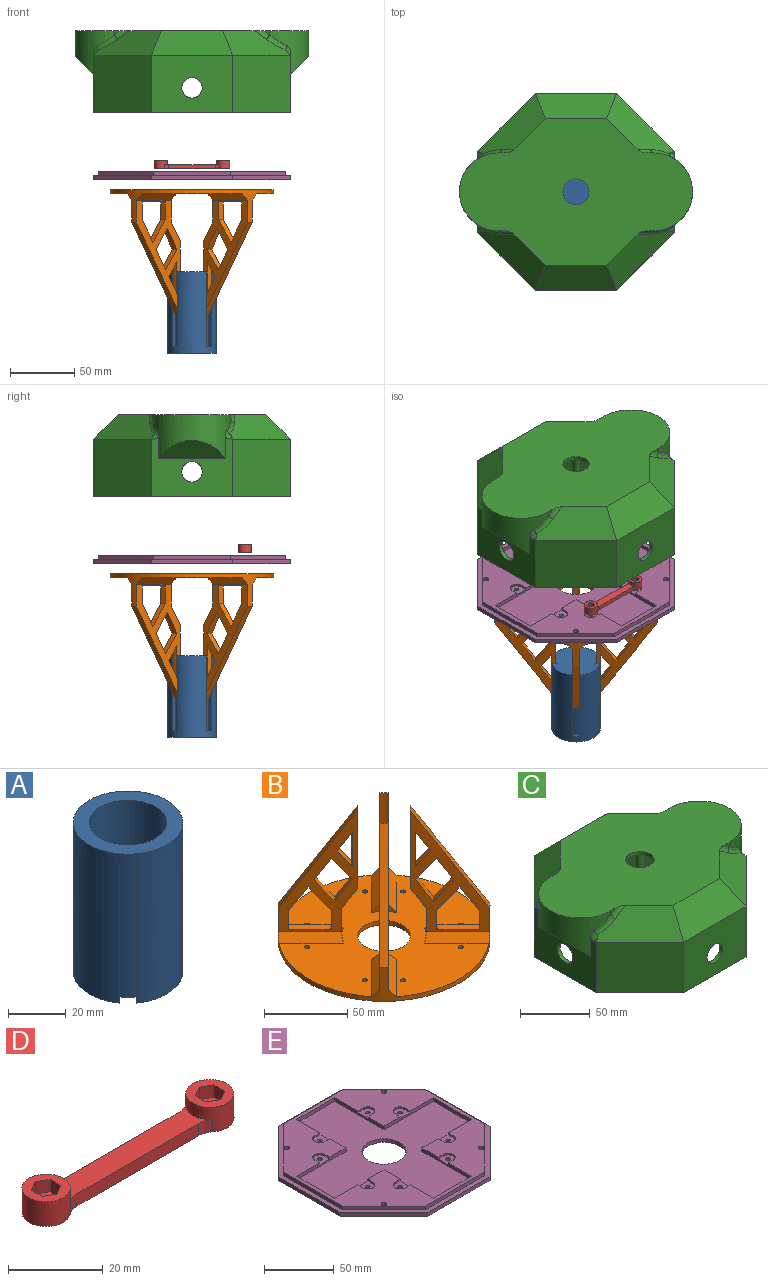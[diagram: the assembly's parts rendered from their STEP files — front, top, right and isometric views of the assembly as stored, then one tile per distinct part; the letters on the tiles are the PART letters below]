
ASSEMBLY  parts=5 mates=4
PART A: 21 faces, bbox 38.1x38.1x63.5 mm
  f0: plane 58.42x2.46mm, normal (0.71,0.71,0), area 203mm2, adj f2,f12,f15,f20
  f1: plane 58.42x2.46mm, normal (-0.71,-0.71,0), area 203mm2, adj f2,f12,f15,f20
  f2: cylinder r=15.62mm len=58.42mm, axis (0,0,-1), area 328.2mm2, adj f0,f1,f15,f20
  f3: plane 58.42x2.46mm, normal (0.71,-0.71,0), area 203mm2, adj f5,f12,f15,f19
  f4: plane 58.42x2.46mm, normal (-0.71,0.71,0), area 203mm2, adj f5,f12,f15,f19
  f5: cylinder r=15.62mm len=58.42mm, axis (0,0,-1), area 328.2mm2, adj f3,f4,f15,f19
  f6: plane 58.42x2.46mm, normal (-0.71,-0.71,0), area 203mm2, adj f8,f12,f15,f18
  f7: plane 58.42x2.46mm, normal (0.71,0.71,0), area 203mm2, adj f8,f12,f15,f18
  f8: cylinder r=15.62mm len=58.42mm, axis (0,0,-1), area 328.2mm2, adj f6,f7,f15,f18
  f9: plane 58.42x2.46mm, normal (0.71,-0.71,0), area 203mm2, adj f11,f12,f15,f17
  f10: plane 58.42x2.46mm, normal (-0.71,0.71,0), area 203mm2, adj f11,f12,f15,f17
  f11: cylinder r=15.62mm len=58.42mm, axis (0,0,-1), area 328.2mm2, adj f9,f10,f15,f17
  f12: cylinder r=19.05mm len=63.5mm, axis (0,0,-1), area 6290.1mm2, adj f0,f1,f3,f4,f6,f7,f9,f10
  f13: cylinder r=13.46mm len=58.42mm, axis (0,0,-1), area 4941.4mm2, adj f14,f16
  f14: plane 38.1x38.1mm, normal (0,0,1), area 570.8mm2, adj f12,f13
  f15: plane 38.1x38.1mm, normal (0,0,-1), area 1063.1mm2, adj f0,f1,f2,f3,f4,f5,f6,f7
  f16: plane 26.92x26.92mm, normal (0,0,1), area 569.3mm2, adj f13
  f17: plane 6.41x6.41mm, normal (0,0,-1), area 19.2mm2, adj f9,f10,f11,f12
  f18: plane 6.41x6.41mm, normal (0,0,-1), area 19.2mm2, adj f6,f7,f8,f12
  f19: plane 6.41x6.41mm, normal (0,0,-1), area 19.2mm2, adj f3,f4,f5,f12
  f20: plane 6.41x6.41mm, normal (0,0,-1), area 19.2mm2, adj f0,f1,f2,f12
PART B: 92 faces, bbox 127.6x127.6x97.7 mm
  f0: plane 89.46x34.37mm, normal (0.71,0.71,0), area 1250.3mm2, adj f9,f13,f17,f28,f29,f30,f31,f32
  f1: plane 88.87x33.78mm, normal (0.71,-0.71,0), area 1250.3mm2, adj f10,f16,f17,f33,f68,f69,f70,f71
  f2: plane 89.46x34.37mm, normal (-0.71,0.71,0), area 1250.3mm2, adj f10,f16,f17,f33,f68,f69,f70,f71
  f3: plane 88.87x33.78mm, normal (0.71,0.71,0), area 1250.3mm2, adj f11,f15,f17,f34,f56,f57,f58,f59
  f4: plane 89.46x34.37mm, normal (-0.71,-0.71,0), area 1250.3mm2, adj f11,f15,f17,f34,f56,f57,f58,f59
  f5: plane 88.87x33.78mm, normal (-0.71,0.71,0), area 1250.3mm2, adj f12,f14,f17,f35,f44,f45,f46,f47
  f6: plane 89.46x34.37mm, normal (0.71,-0.71,0), area 1250.3mm2, adj f12,f14,f17,f35,f44,f45,f46,f47
  f7: plane 88.87x33.78mm, normal (-0.71,-0.71,0), area 1250.3mm2, adj f9,f13,f17,f28,f29,f30,f31,f32
  f8: plane 127x127mm, normal (0,0,1), area 9480.5mm2, adj f17,f18,f19,f20,f21,f22,f23,f24
  f9: revolved ~14.57x12.25mm, area 92.3mm2, adj f0,f7,f32,f83
  f10: revolved ~14.57x12.25mm, area 92.3mm2, adj f1,f2,f33,f80
  f11: revolved ~14.57x12.25mm, area 92.3mm2, adj f3,f4,f34,f81
  f12: revolved ~14.57x12.25mm, area 92.3mm2, adj f5,f6,f35,f82
  f13: revolved ~71.93x46.32mm, area 438.7mm2, adj f0,f7,f17,f83
  f14: revolved ~71.93x46.32mm, area 438.7mm2, adj f5,f6,f17,f82
  f15: revolved ~71.93x46.32mm, area 438.7mm2, adj f3,f4,f17,f81
  f16: revolved ~71.93x46.32mm, area 438.7mm2, adj f1,f2,f17,f80
  f17: cylinder r=63.5mm len=127mm, axis (0,0,-1), area 1818mm2, adj f0,f1,f2,f3,f4,f5,f6,f7
  f18: cylinder r=1.59mm len=3.18mm, axis (0,0,-1), area 31.7mm2, adj f8,f26
  f19: cylinder r=1.59mm len=3.18mm, axis (0,0,-1), area 31.7mm2, adj f8,f26
  f20: cylinder r=1.59mm len=3.18mm, axis (0,0,-1), area 31.7mm2, adj f8,f26
  f21: cylinder r=1.59mm len=3.18mm, axis (0,0,-1), area 31.7mm2, adj f8,f26
  f22: cylinder r=1.59mm len=3.18mm, axis (0,0,-1), area 31.7mm2, adj f8,f26
  f23: cylinder r=1.59mm len=3.18mm, axis (0,0,-1), area 31.7mm2, adj f8,f26
  f24: cylinder r=1.59mm len=3.18mm, axis (0,0,-1), area 31.7mm2, adj f8,f26
  f25: cylinder r=1.59mm len=3.18mm, axis (0,0,-1), area 31.7mm2, adj f8,f26
  f26: plane 127x127mm, normal (0,0,-1), area 11812.6mm2, adj f17,f18,f19,f20,f21,f22,f23,f24
  f27: cylinder r=15.88mm len=31.75mm, axis (0,0,-1), area 316.7mm2, adj f8,f26
  f28: revolved ~15.83x12.12mm, area 97.9mm2, adj f0,f7,f29,f31
  f29: revolved ~15.82x13.69mm, area 104mm2, adj f0,f7,f28,f30
  f30: revolved ~15.83x12.71mm, area 99.6mm2, adj f0,f7,f29,f31
  f31: revolved ~15.82x14.31mm, area 101.9mm2, adj f0,f7,f28,f30
  f32: cylinder r=25.48mm len=22.02mm, axis (0,0,1), area 138.4mm2, adj f0,f7,f8,f9,f88,f89
  f33: cylinder r=25.48mm len=22.02mm, axis (0,0,1), area 138.4mm2, adj f1,f2,f8,f10,f86,f87
  f34: cylinder r=25.48mm len=22.02mm, axis (0,0,1), area 138.4mm2, adj f3,f4,f8,f11,f84,f85
  f35: cylinder r=25.48mm len=22.02mm, axis (0,0,1), area 138.4mm2, adj f5,f6,f8,f12,f90,f91
  f36: revolved ~11.32x11.26mm, area 74.7mm2, adj f0,f7,f37,f38
  f37: cylinder r=19.22mm len=24.62mm, axis (0,0,1), area 125.4mm2, adj f0,f7,f36,f38
  f38: revolved ~13.3x11.26mm, area 83.1mm2, adj f0,f7,f36,f37
  f39: revolved ~17.58x14.72mm, area 115.7mm2, adj f0,f7,f40,f43
  f40: revolved ~17.58x12.72mm, area 108.1mm2, adj f0,f7,f39,f41
  f41: cylinder r=57.16mm len=13.76mm, axis (0,0,1), area 69.9mm2, adj f0,f7,f40,f42
  f42: plane 21.55x21.55mm, normal (0,0,1), area 128.9mm2, adj f0,f7,f41,f43
  f43: cylinder r=31.8mm len=13.76mm, axis (0,0,1), area 70mm2, adj f0,f7,f39,f42
  f44: revolved ~15.83x12.12mm, area 97.9mm2, adj f5,f6,f45,f47
  f45: revolved ~15.82x13.69mm, area 104mm2, adj f5,f6,f44,f46
  f46: revolved ~15.83x12.71mm, area 99.6mm2, adj f5,f6,f45,f47
  f47: revolved ~15.82x14.31mm, area 101.9mm2, adj f5,f6,f44,f46
  f48: revolved ~11.32x11.26mm, area 74.7mm2, adj f5,f6,f49,f50
  f49: cylinder r=19.22mm len=24.62mm, axis (0,0,1), area 125.4mm2, adj f5,f6,f48,f50
  f50: revolved ~13.3x11.26mm, area 83.1mm2, adj f5,f6,f48,f49
  f51: revolved ~17.58x14.72mm, area 115.7mm2, adj f5,f6,f52,f55
  f52: revolved ~17.58x12.72mm, area 108.1mm2, adj f5,f6,f51,f53
  f53: cylinder r=57.16mm len=13.76mm, axis (0,0,1), area 69.9mm2, adj f5,f6,f52,f54
  f54: plane 21.55x21.55mm, normal (0,0,1), area 128.9mm2, adj f5,f6,f53,f55
  f55: cylinder r=31.8mm len=13.76mm, axis (0,0,1), area 70mm2, adj f5,f6,f51,f54
  f56: revolved ~15.83x12.12mm, area 97.9mm2, adj f3,f4,f57,f59
  f57: revolved ~15.82x13.69mm, area 104mm2, adj f3,f4,f56,f58
  f58: revolved ~15.83x12.71mm, area 99.6mm2, adj f3,f4,f57,f59
  f59: revolved ~15.82x14.31mm, area 101.9mm2, adj f3,f4,f56,f58
  f60: revolved ~11.32x11.26mm, area 74.7mm2, adj f3,f4,f61,f62
  f61: cylinder r=19.22mm len=24.62mm, axis (0,0,1), area 125.4mm2, adj f3,f4,f60,f62
  f62: revolved ~13.3x11.26mm, area 83.1mm2, adj f3,f4,f60,f61
  f63: revolved ~17.58x14.72mm, area 115.7mm2, adj f3,f4,f64,f67
  f64: revolved ~17.58x12.72mm, area 108.1mm2, adj f3,f4,f63,f65
  f65: cylinder r=57.16mm len=13.76mm, axis (0,0,1), area 69.9mm2, adj f3,f4,f64,f66
  f66: plane 21.55x21.55mm, normal (0,0,1), area 128.9mm2, adj f3,f4,f65,f67
  f67: cylinder r=31.8mm len=13.76mm, axis (0,0,1), area 70mm2, adj f3,f4,f63,f66
  f68: revolved ~15.82x14.31mm, area 101.9mm2, adj f1,f2,f69,f71
  f69: revolved ~15.83x12.71mm, area 99.6mm2, adj f1,f2,f68,f70
  f70: revolved ~15.82x13.69mm, area 104mm2, adj f1,f2,f69,f71
  f71: revolved ~15.83x12.12mm, area 97.9mm2, adj f1,f2,f68,f70
  f72: revolved ~13.3x11.26mm, area 83.1mm2, adj f1,f2,f73,f74
  f73: cylinder r=19.22mm len=24.62mm, axis (0,0,1), area 125.4mm2, adj f1,f2,f72,f74
  f74: revolved ~11.32x11.26mm, area 74.7mm2, adj f1,f2,f72,f73
  f75: cylinder r=31.8mm len=13.76mm, axis (0,0,1), area 70mm2, adj f1,f2,f76,f79
  f76: plane 21.55x21.55mm, normal (0,0,1), area 128.9mm2, adj f1,f2,f75,f77
  f77: cylinder r=57.16mm len=13.76mm, axis (0,0,1), area 69.9mm2, adj f1,f2,f76,f78
  f78: revolved ~17.58x12.72mm, area 108.1mm2, adj f1,f2,f77,f79
  f79: revolved ~17.58x14.72mm, area 115.7mm2, adj f1,f2,f75,f78
  f80: cylinder r=15.88mm len=57.36mm, axis (0,0,-1), area 292.6mm2, adj f1,f2,f10,f16
  f81: cylinder r=15.88mm len=57.36mm, axis (0,0,-1), area 292.6mm2, adj f3,f4,f11,f15
  f82: cylinder r=15.88mm len=57.36mm, axis (0,0,-1), area 292.6mm2, adj f5,f6,f12,f14
  f83: cylinder r=15.88mm len=57.36mm, axis (0,0,-1), area 292.6mm2, adj f0,f7,f9,f13
  f84: plane 31.32x30.3mm, normal (-0.5,-0.5,0.71), area 275.6mm2, adj f4,f8,f17,f34
  f85: plane 31.32x30.3mm, normal (0.5,0.5,0.71), area 275.6mm2, adj f3,f8,f17,f34
  f86: plane 31.32x30.3mm, normal (-0.5,0.5,0.71), area 275.6mm2, adj f2,f8,f17,f33
  f87: plane 31.32x30.3mm, normal (0.5,-0.5,0.71), area 275.6mm2, adj f1,f8,f17,f33
  f88: plane 31.32x30.3mm, normal (0.5,0.5,0.71), area 275.6mm2, adj f0,f8,f17,f32
  f89: plane 31.32x30.3mm, normal (-0.5,-0.5,0.71), area 275.6mm2, adj f7,f8,f17,f32
  f90: plane 31.32x30.3mm, normal (-0.5,0.5,0.71), area 275.6mm2, adj f5,f8,f17,f35
  f91: plane 31.32x30.3mm, normal (0.5,-0.5,0.71), area 275.6mm2, adj f6,f8,f17,f35
PART C: 114 faces, bbox 182x153.4x68.1 mm
  f0: plane 23.42x20.32mm, normal (0,0,-1), area 38.2mm2, adj f1,f24,f25,f82,f99
  f1: plane 49.08x44.17mm, normal (0.5,0.5,-0.71), area 1020.5mm2, adj f0,f6,f68,f69,f82,f83,f84,f99
  f2: plane 98.78x20.07mm, normal (0,0,-1), area 149.3mm2, adj f3,f5,f26,f27,f28,f61,f94,f96
  f3: plane 49.07x44.17mm, normal (0.5,-0.5,-0.71), area 1020.5mm2, adj f2,f9,f61,f62,f69,f80,f81,f96
  f4: plane 23.42x20.32mm, normal (0,0,-1), area 38.2mm2, adj f5,f21,f28,f60,f93
  f5: plane 49.08x44.17mm, normal (-0.5,-0.5,-0.71), area 1020.5mm2, adj f2,f4,f60,f61,f69,f78,f79,f93
  f6: plane 98.78x20.07mm, normal (0,0,-1), area 149.3mm2, adj f1,f7,f22,f23,f24,f68,f90,f100
  f7: plane 49.07x44.17mm, normal (-0.5,0.5,-0.71), area 1020.5mm2, adj f6,f8,f59,f68,f69,f76,f77,f90
  f8: plane 23.42x20.32mm, normal (0,0,-1), area 38.2mm2, adj f7,f21,f22,f59,f91
  f9: plane 23.42x20.32mm, normal (0,0,-1), area 38.2mm2, adj f3,f25,f26,f62,f97
  f10: plane 52.98x47.33mm, normal (0.5,-0.5,0.71), area 1325.9mm2, adj f14,f31,f32,f37,f46,f47,f48
  f11: plane 2.19x2.13mm, normal (0.71,0,0.71), area 3.2mm2, adj f15,f33,f49
  f12: plane 2.19x2.13mm, normal (-0.71,0,0.71), area 3.2mm2, adj f13,f19,f55
  f13: plane 52.98x47.34mm, normal (-0.5,-0.5,0.71), area 1325.9mm2, adj f12,f20,f31,f37,f55,f56,f57
  f14: plane 44.64x44.64mm, normal (0.71,-0.71,0), area 2806mm2, adj f10,f15,f29,f30
  f15: plane 63.13x48.96mm, normal (1,0,0), area 1832.7mm2, adj f11,f14,f16,f30,f32,f41,f44,f46
  f16: plane 44.64x44.64mm, normal (0.71,0.71,0), area 2806mm2, adj f15,f17,f30,f33
  f17: plane 63.13x44.45mm, normal (0,1,0), area 2608mm2, adj f16,f18,f30,f34,f86
  f18: plane 44.64x44.64mm, normal (-0.71,0.71,0), area 2806mm2, adj f17,f19,f30,f35
  f19: plane 63.13x48.96mm, normal (-1,0,0), area 1832.7mm2, adj f12,f18,f20,f30,f36,f38,f45,f52
  f20: plane 44.64x44.64mm, normal (-0.71,-0.71,0), area 2806mm2, adj f13,f19,f29,f30
  f21: plane 60.5x50.93mm, normal (-1,0,0), area 2499.7mm2, adj f4,f8,f22,f28,f30,f59,f60,f67
  f22: plane 44.45x42.78mm, normal (-0.71,0.71,0), area 2427mm2, adj f6,f8,f21,f23,f30,f90,f91,f105
  f23: plane 60.5x44.45mm, normal (0,1,0), area 2491.1mm2, adj f6,f22,f24,f30,f85
  f24: plane 44.45x42.78mm, normal (0.71,0.71,0), area 2427mm2, adj f0,f6,f23,f25,f30,f99,f100,f102
  f25: plane 60.5x50.93mm, normal (1,0,0), area 2499.7mm2, adj f0,f9,f24,f26,f30,f58,f62,f70
  f26: plane 44.45x42.78mm, normal (0.71,-0.71,0), area 2427mm2, adj f2,f9,f25,f27,f30,f96,f97,f103
  f27: plane 60.5x44.45mm, normal (0,-1,0), area 2491.1mm2, adj f2,f26,f28,f30,f86
  f28: plane 44.45x42.78mm, normal (-0.71,-0.71,0), area 2427mm2, adj f2,f4,f21,f27,f30,f93,f94,f104
  f29: plane 63.13x44.45mm, normal (0,-1,0), area 2608mm2, adj f14,f20,f30,f31,f85
  f30: plane 152.4x152.4mm, normal (0,0,-1), area 1570mm2, adj f14,f15,f16,f17,f18,f19,f20,f21
  f31: plane 63.13x19.05mm, normal (0,-0.71,0.71), area 1488.1mm2, adj f10,f13,f29,f37
  f32: plane 2.19x2.13mm, normal (0.71,0,0.71), area 3.2mm2, adj f10,f15,f46
  f33: plane 52.98x47.34mm, normal (0.5,0.5,0.71), area 1325.9mm2, adj f11,f16,f34,f37,f49,f50,f51
  f34: plane 63.13x19.05mm, normal (0,0.71,0.71), area 1488.1mm2, adj f17,f33,f35,f37
  f35: plane 52.98x47.33mm, normal (-0.5,0.5,0.71), area 1325.9mm2, adj f18,f34,f36,f37,f52,f53,f54
  f36: plane 2.19x2.13mm, normal (-0.71,0,0.71), area 3.2mm2, adj f19,f35,f52
  f37: plane 181.96x115.28mm, normal (0,0,1), area 13833.8mm2, adj f10,f13,f31,f33,f34,f35,f38,f39
  f38: cylinder r=30.16mm len=60.33mm, axis (0,0,1), area 1810.7mm2, adj f19,f37,f39,f40,f45,f52,f53,f55
  f39: plane 4.59x3.24mm, normal (0,-1,0), area 7.4mm2, adj f37,f38,f57
  f40: plane 4.59x3.24mm, normal (0,1,0), area 7.4mm2, adj f37,f38,f54
  f41: cylinder r=30.16mm len=60.33mm, axis (0,0,1), area 1810.7mm2, adj f15,f37,f42,f43,f44,f46,f47,f49
  f42: plane 4.59x3.24mm, normal (0,-1,0), area 7.4mm2, adj f37,f41,f48
  f43: plane 4.59x3.24mm, normal (0,1,0), area 7.4mm2, adj f37,f41,f51
  f44: plane 51.29x14.29mm, normal (0.71,0,-0.71), area 732.1mm2, adj f15,f41
  f45: plane 51.29x14.29mm, normal (-0.71,0,-0.71), area 732.1mm2, adj f19,f38
  f46: bspline ~7.61x6.56mm, area 28.3mm2, adj f10,f15,f32,f41,f47
  f47: bspline ~25.08x17.8mm, area 80.8mm2, adj f10,f41,f46,f48
  f48: cylinder r=5.08mm len=12.21mm, axis (0.82,0,-0.58), area 46.4mm2, adj f10,f37,f42,f47
  f49: bspline ~7.61x6.56mm, area 28.3mm2, adj f11,f15,f33,f41,f50
  f50: bspline ~25.08x17.8mm, area 80.8mm2, adj f33,f41,f49,f51
  f51: cylinder r=5.08mm len=12.21mm, axis (-0.82,0,0.58), area 46.4mm2, adj f33,f37,f43,f50
  f52: bspline ~7.61x6.56mm, area 28.3mm2, adj f19,f35,f36,f38,f53
  f53: bspline ~25.08x17.8mm, area 80.8mm2, adj f35,f38,f52,f54
  f54: cylinder r=5.08mm len=12.21mm, axis (-0.82,0,-0.58), area 46.4mm2, adj f35,f37,f40,f53
  f55: bspline ~7.61x6.56mm, area 28.3mm2, adj f12,f13,f19,f38,f56
  f56: bspline ~25.08x17.8mm, area 80.8mm2, adj f13,f38,f55,f57
  f57: cylinder r=5.08mm len=12.21mm, axis (0.82,0,0.58), area 46.4mm2, adj f13,f37,f39,f56
  f58: plane 47.63x3.18mm, normal (0,0,1), area 145.2mm2, adj f25,f66,f70
  f59: bspline ~16.45x12.45mm, area 21.5mm2, adj f7,f8,f21,f73,f76
  f60: bspline ~16.45x12.45mm, area 21.5mm2, adj f4,f5,f21,f73,f78
  f61: plane 59.41x15.88mm, normal (0,-0.71,-0.71), area 1186.1mm2, adj f2,f3,f5,f69
  f62: bspline ~16.45x12.45mm, area 21.5mm2, adj f3,f9,f25,f70,f80
  f63: plane 43.65x11.11mm, normal (0.71,0,0.71), area 480.2mm2, adj f66,f70
  f64: plane 43.65x11.11mm, normal (-0.71,0,0.71), area 480.2mm2, adj f65,f73
  f65: plane 43.65x10.75mm, normal (1,0,0), area 469.2mm2, adj f64,f67,f73
  f66: plane 43.65x10.75mm, normal (-1,0,0), area 469.2mm2, adj f58,f63,f70
  f67: plane 47.63x3.18mm, normal (0,0,1), area 145.2mm2, adj f21,f65,f73
  f68: plane 59.41x15.88mm, normal (0,0.71,-0.71), area 1186.1mm2, adj f1,f6,f7,f69
  f69: plane 174.63x111.67mm, normal (0,0,-1), area 12834.3mm2, adj f1,f3,f5,f7,f61,f68,f70,f71
  f70: cylinder r=26.99mm len=53.98mm, axis (0,0,1), area 1236.1mm2, adj f25,f58,f62,f63,f66,f69,f71,f72
  f71: plane 0.1x0.07mm, normal (0,1,0), area 0mm2, adj f69,f70,f84
  f72: plane 0.1x0.07mm, normal (0,-1,0), area 0mm2, adj f69,f70,f81
  f73: cylinder r=26.99mm len=53.98mm, axis (0,0,1), area 1236.1mm2, adj f21,f59,f60,f64,f65,f67,f69,f74
  f74: plane 0.1x0.07mm, normal (0,1,0), area 0mm2, adj f69,f73,f77
  f75: plane 0.1x0.07mm, normal (0,-1,0), area 0mm2, adj f69,f73,f79
  f76: bspline ~25.08x20.04mm, area 124.4mm2, adj f7,f59,f73,f77
  f77: cylinder r=8.26mm len=12.48mm, axis (0.82,0,-0.58), area 49.2mm2, adj f7,f69,f74,f76
  f78: bspline ~25.08x20.04mm, area 124.4mm2, adj f5,f60,f73,f79
  f79: cylinder r=8.26mm len=12.48mm, axis (-0.82,0,0.58), area 49.2mm2, adj f5,f69,f75,f78
  f80: bspline ~25.08x20.04mm, area 124.4mm2, adj f3,f62,f70,f81
  f81: cylinder r=8.26mm len=12.48mm, axis (-0.82,0,-0.58), area 49.2mm2, adj f3,f69,f72,f80
  f82: bspline ~16.45x12.45mm, area 21.5mm2, adj f0,f1,f25,f70,f83
  f83: bspline ~25.08x20.04mm, area 124.4mm2, adj f1,f70,f82,f84
  f84: cylinder r=8.26mm len=12.48mm, axis (0.82,0,0.58), area 49.2mm2, adj f1,f69,f71,f83
  f85: cylinder r=7.94mm len=15.88mm, axis (0,-1,0), area 158.3mm2, adj f23,f29
  f86: cylinder r=7.94mm len=15.88mm, axis (0,-1,0), area 158.3mm2, adj f17,f27
  f87: cylinder r=7.94mm len=15.88mm, axis (1,0,0), area 158.3mm2, adj f19,f25
  f88: cylinder r=7.94mm len=15.88mm, axis (1,0,0), area 158.3mm2, adj f15,f21
  f89: cylinder r=10.16mm len=20.32mm, axis (0,0,1), area 202.7mm2, adj f37,f69
  f90: plane 43.14x2.25mm, normal (-0.71,-0.71,0), area 132.8mm2, adj f6,f7,f22,f92,f105
  f91: plane 43.11x2.23mm, normal (0.71,0.71,0), area 131.6mm2, adj f7,f8,f22,f92,f105
  f92: cylinder r=3.17mm len=46.32mm, axis (0,0,-1), area 451.6mm2, adj f7,f90,f91,f105
  f93: plane 43.14x2.25mm, normal (0.71,-0.71,0), area 132.8mm2, adj f4,f5,f28,f95,f104
  f94: plane 43.11x2.23mm, normal (-0.71,0.71,0), area 131.6mm2, adj f2,f5,f28,f95,f104
  f95: cylinder r=3.17mm len=46.32mm, axis (0,0,-1), area 451.6mm2, adj f5,f93,f94,f104
  f96: plane 43.14x2.25mm, normal (0.71,0.71,0), area 132.8mm2, adj f2,f3,f26,f98,f103
  f97: plane 43.11x2.23mm, normal (-0.71,-0.71,0), area 131.6mm2, adj f3,f9,f26,f98,f103
  f98: cylinder r=3.17mm len=46.32mm, axis (0,0,-1), area 451.6mm2, adj f3,f96,f97,f103
  f99: plane 43.14x2.25mm, normal (-0.71,0.71,0), area 132.8mm2, adj f0,f1,f24,f101,f102
  f100: plane 43.11x2.23mm, normal (0.71,-0.71,0), area 131.6mm2, adj f1,f6,f24,f101,f102
  f101: cylinder r=3.17mm len=46.32mm, axis (0,0,-1), area 451.6mm2, adj f1,f99,f100,f102
  f102: plane 7.67x7.67mm, normal (0,0,-1), area 28.1mm2, adj f24,f99,f100,f101,f107
  f103: plane 7.67x7.67mm, normal (0,0,-1), area 28.1mm2, adj f26,f96,f97,f98,f109
  f104: plane 7.67x7.67mm, normal (0,0,-1), area 28.1mm2, adj f28,f93,f94,f95,f111
  f105: plane 7.67x7.67mm, normal (0,0,-1), area 28.1mm2, adj f22,f90,f91,f92,f113
  f106: plane 3.18x3.18mm, normal (0.5,0.5,-0.71), area 11.2mm2, adj f107
  f107: cylinder r=1.59mm len=44.74mm, axis (0,0,-1), area 430.3mm2, adj f102,f106
  f108: plane 3.18x3.18mm, normal (0.5,-0.5,-0.71), area 11.2mm2, adj f109
  f109: cylinder r=1.59mm len=44.74mm, axis (0,0,-1), area 430.3mm2, adj f103,f108
  f110: plane 3.18x3.18mm, normal (-0.5,-0.5,-0.71), area 11.2mm2, adj f111
  f111: cylinder r=1.59mm len=44.74mm, axis (0,0,-1), area 430.3mm2, adj f104,f110
  f112: plane 3.18x3.18mm, normal (-0.5,0.5,-0.71), area 11.2mm2, adj f113
  f113: cylinder r=1.59mm len=44.74mm, axis (0,0,-1), area 430.3mm2, adj f105,f112
PART D: 28 faces, bbox 58.9x10.2x6.4 mm
  f0: cylinder r=1.59mm len=3.18mm, axis (0,0,-1), area 31.7mm2, adj f7,f23
  f1: cylinder r=1.59mm len=3.18mm, axis (0,0,-1), area 31.7mm2, adj f7,f16
  f2: plane 10.16x10.16mm, normal (0,0,1), area 54.5mm2, adj f8,f17,f18,f19,f20,f21,f22
  f3: plane 10.16x10.16mm, normal (0,0,1), area 54.5mm2, adj f9,f10,f11,f12,f13,f14,f15
  f4: plane 36.25x3.18mm, normal (0,1,0), area 115.1mm2, adj f6,f7,f24,f26
  f5: plane 36.25x3.18mm, normal (0,-1,0), area 115.1mm2, adj f6,f7,f25,f27
  f6: plane 42.51x8mm, normal (0,0,1), area 230.9mm2, adj f4,f5,f8,f9,f24,f25,f26,f27
  f7: plane 58.93x10.16mm, normal (0,0,-1), area 377.2mm2, adj f0,f1,f4,f5,f8,f9,f24,f25
  f8: cylinder r=5.08mm len=10.16mm, axis (0,0,-1), area 173.4mm2, adj f2,f6,f7,f26,f27
  f9: cylinder r=5.08mm len=10.16mm, axis (0,0,-1), area 173.4mm2, adj f3,f6,f7,f24,f25
  f10: plane 3.2x3.18mm, normal (1,0,0), area 10.2mm2, adj f3,f11,f15,f16
  f11: plane 3.18x2.77mm, normal (0.5,0.87,0), area 10.2mm2, adj f3,f10,f12,f16
  f12: plane 3.18x2.77mm, normal (-0.5,0.87,0), area 10.2mm2, adj f3,f11,f13,f16
  f13: plane 3.2x3.18mm, normal (-1,0,0), area 10.2mm2, adj f3,f12,f14,f16
  f14: plane 3.18x2.77mm, normal (-0.5,-0.87,0), area 10.2mm2, adj f3,f13,f15,f16
  f15: plane 3.18x2.77mm, normal (0.5,-0.87,0), area 10.2mm2, adj f3,f10,f14,f16
  f16: plane 6.39x5.54mm, normal (0,0,1), area 18.6mm2, adj f1,f10,f11,f12,f13,f14,f15
  f17: plane 3.18x2.77mm, normal (0.5,0.87,0), area 10.2mm2, adj f2,f18,f22,f23
  f18: plane 3.18x2.77mm, normal (-0.5,0.87,0), area 10.2mm2, adj f2,f17,f19,f23
  f19: plane 3.2x3.18mm, normal (-1,0,0), area 10.2mm2, adj f2,f18,f20,f23
  f20: plane 3.18x2.77mm, normal (-0.5,-0.87,0), area 10.2mm2, adj f2,f19,f21,f23
  f21: plane 3.18x2.77mm, normal (0.5,-0.87,0), area 10.2mm2, adj f2,f20,f22,f23
  f22: plane 3.2x3.18mm, normal (1,0,0), area 10.2mm2, adj f2,f17,f21,f23
  f23: plane 6.39x5.54mm, normal (0,0,1), area 18.6mm2, adj f0,f17,f18,f19,f20,f21,f22
  f24: cylinder r=5.08mm len=3.18mm, axis (0,0,-1), area 10.7mm2, adj f4,f6,f7,f9
  f25: cylinder r=5.08mm len=3.18mm, axis (0,0,-1), area 10.7mm2, adj f5,f6,f7,f9
  f26: cylinder r=5.08mm len=3.18mm, axis (0,0,-1), area 10.7mm2, adj f4,f6,f7,f8
  f27: cylinder r=5.08mm len=3.18mm, axis (0,0,-1), area 10.7mm2, adj f5,f6,f7,f8
PART E: 81 faces, bbox 152.4x152.4x6.4 mm
  f0: cylinder r=1.59mm len=4.76mm, axis (0,0,-1), area 47.5mm2, adj f18,f71
  f1: cylinder r=1.59mm len=4.76mm, axis (0,0,-1), area 47.5mm2, adj f18,f67
  f2: cylinder r=1.59mm len=4.76mm, axis (0,0,-1), area 47.5mm2, adj f18,f63
  f3: cylinder r=1.59mm len=4.76mm, axis (0,0,-1), area 47.5mm2, adj f18,f56
  f4: cylinder r=1.59mm len=4.76mm, axis (0,0,-1), area 47.5mm2, adj f18,f55
  f5: cylinder r=1.59mm len=4.76mm, axis (0,0,-1), area 47.5mm2, adj f18,f48
  f6: cylinder r=1.59mm len=4.76mm, axis (0,0,-1), area 47.5mm2, adj f18,f44
  f7: cylinder r=1.59mm len=4.76mm, axis (0,0,-1), area 47.5mm2, adj f18,f40
  f8: plane 145.03x145.03mm, normal (0,0,1), area 7418.7mm2, adj f19,f20,f21,f22,f23,f24,f25,f26
  f9: plane 152.4x152.4mm, normal (0,0,1), area 1815mm2, adj f10,f11,f12,f13,f14,f15,f16,f17
  f10: plane 44.64x44.64mm, normal (0.71,-0.71,0), area 200.4mm2, adj f9,f11,f17,f18
  f11: plane 63.13x3.18mm, normal (1,0,0), area 200.4mm2, adj f9,f10,f12,f18
  f12: plane 44.64x44.64mm, normal (0.71,0.71,0), area 200.4mm2, adj f9,f11,f13,f18
  f13: plane 63.13x3.18mm, normal (0,1,0), area 200.4mm2, adj f9,f12,f14,f18
  f14: plane 44.64x44.64mm, normal (-0.71,0.71,0), area 200.4mm2, adj f9,f13,f15,f18
  f15: plane 63.13x3.18mm, normal (-1,0,0), area 200.4mm2, adj f9,f14,f16,f18
  f16: plane 44.64x44.64mm, normal (-0.71,-0.71,0), area 200.4mm2, adj f9,f15,f17,f18
  f17: plane 63.13x3.18mm, normal (0,-1,0), area 200.4mm2, adj f9,f10,f16,f18
  f18: plane 152.4x152.4mm, normal (0,0,-1), area 18248.8mm2, adj f0,f1,f2,f3,f4,f5,f6,f7
  f19: plane 60.08x3.18mm, normal (0,1,0), area 190.7mm2, adj f8,f9,f20,f26
  f20: plane 42.48x42.48mm, normal (-0.71,0.71,0), area 190.7mm2, adj f8,f9,f19,f21
  f21: plane 60.08x3.18mm, normal (-1,0,0), area 190.7mm2, adj f8,f9,f20,f22
  f22: plane 42.48x42.48mm, normal (-0.71,-0.71,0), area 190.7mm2, adj f8,f9,f21,f23
  f23: plane 60.08x3.18mm, normal (0,-1,0), area 190.7mm2, adj f8,f9,f22,f24
  f24: plane 42.48x42.48mm, normal (0.71,-0.71,0), area 190.7mm2, adj f8,f9,f23,f25
  f25: plane 60.08x3.18mm, normal (1,0,0), area 190.7mm2, adj f8,f9,f24,f26
  f26: plane 42.48x42.48mm, normal (0.71,0.71,0), area 190.7mm2, adj f8,f9,f19,f25
  f27: plane 50.04x3.18mm, normal (0,1,0), area 142.7mm2, adj f8,f28,f38,f39,f52,f54,f55
  f28: plane 50.04x3.18mm, normal (1,0,0), area 142.7mm2, adj f8,f27,f29,f39,f56,f57,f58
  f29: plane 38.61x3.18mm, normal (0,1,0), area 122.6mm2, adj f8,f28,f30,f39
  f30: plane 50.04x3.18mm, normal (-1,0,0), area 142.7mm2, adj f8,f29,f31,f39,f60,f62,f63
  f31: plane 50.04x3.18mm, normal (0,1,0), area 142.7mm2, adj f8,f30,f32,f39,f64,f66,f67
  f32: plane 38.61x3.18mm, normal (-1,0,0), area 122.6mm2, adj f8,f31,f33,f39
  f33: plane 50.04x3.18mm, normal (0,-1,0), area 142.7mm2, adj f8,f32,f34,f39,f40,f41,f42
  f34: plane 50.04x3.18mm, normal (-1,0,0), area 142.7mm2, adj f8,f33,f35,f39,f68,f69,f71
  f35: plane 38.61x3.18mm, normal (0,-1,0), area 122.6mm2, adj f8,f34,f36,f39
  f36: plane 50.04x3.18mm, normal (1,0,0), area 142.7mm2, adj f8,f35,f37,f39,f44,f45,f46
  f37: plane 50.04x3.18mm, normal (0,-1,0), area 142.7mm2, adj f8,f36,f38,f39,f48,f49,f50
  f38: plane 38.61x3.18mm, normal (1,0,0), area 122.6mm2, adj f8,f27,f37,f39
  f39: plane 138.68x138.68mm, normal (0,0,1), area 8426.3mm2, adj f27,f28,f29,f30,f31,f32,f33,f34
  f40: plane 10.16x10.16mm, normal (0,0,1), area 84.2mm2, adj f7,f33,f41,f42,f43
  f41: plane 5.08x1.59mm, normal (-1,0,0), area 8.1mm2, adj f8,f33,f40,f43
  f42: plane 5.08x1.59mm, normal (1,0,0), area 8.1mm2, adj f8,f33,f40,f43
  f43: cylinder r=5.08mm len=10.16mm, axis (0,0,1), area 25.3mm2, adj f8,f40,f41,f42
  f44: plane 10.16x10.16mm, normal (0,0,1), area 84.2mm2, adj f6,f36,f45,f46,f47
  f45: plane 5.08x1.59mm, normal (0,1,0), area 8.1mm2, adj f8,f36,f44,f47
  f46: plane 5.08x1.59mm, normal (0,-1,0), area 8.1mm2, adj f8,f36,f44,f47
  f47: cylinder r=5.08mm len=10.16mm, axis (0,0,1), area 25.3mm2, adj f8,f44,f45,f46
  f48: plane 10.16x10.16mm, normal (0,0,1), area 84.2mm2, adj f5,f37,f49,f50,f51
  f49: plane 5.08x1.59mm, normal (-1,0,0), area 8.1mm2, adj f8,f37,f48,f51
  f50: plane 5.08x1.59mm, normal (1,0,0), area 8.1mm2, adj f8,f37,f48,f51
  f51: cylinder r=5.08mm len=10.16mm, axis (0,0,1), area 25.3mm2, adj f8,f48,f49,f50
  f52: plane 5.08x1.59mm, normal (1,0,0), area 8.1mm2, adj f8,f27,f53,f55
  f53: cylinder r=5.08mm len=10.16mm, axis (0,0,1), area 25.3mm2, adj f8,f52,f54,f55
  f54: plane 5.08x1.59mm, normal (-1,0,0), area 8.1mm2, adj f8,f27,f53,f55
  f55: plane 10.16x10.16mm, normal (0,0,1), area 84.2mm2, adj f4,f27,f52,f53,f54
  f56: plane 10.16x10.16mm, normal (0,0,1), area 84.2mm2, adj f3,f28,f57,f58,f59
  f57: plane 5.08x1.59mm, normal (0,-1,0), area 8.1mm2, adj f8,f28,f56,f59
  f58: plane 5.08x1.59mm, normal (0,1,0), area 8.1mm2, adj f8,f28,f56,f59
  f59: cylinder r=5.08mm len=10.16mm, axis (0,0,1), area 25.3mm2, adj f8,f56,f57,f58
  f60: plane 5.08x1.59mm, normal (0,1,0), area 8.1mm2, adj f8,f30,f61,f63
  f61: cylinder r=5.08mm len=10.16mm, axis (0,0,1), area 25.3mm2, adj f8,f60,f62,f63
  f62: plane 5.08x1.59mm, normal (0,-1,0), area 8.1mm2, adj f8,f30,f61,f63
  f63: plane 10.16x10.16mm, normal (0,0,1), area 84.2mm2, adj f2,f30,f60,f61,f62
  f64: plane 5.08x1.59mm, normal (1,0,0), area 8.1mm2, adj f8,f31,f65,f67
  f65: cylinder r=5.08mm len=10.16mm, axis (0,0,1), area 25.3mm2, adj f8,f64,f66,f67
  f66: plane 5.08x1.59mm, normal (-1,0,0), area 8.1mm2, adj f8,f31,f65,f67
  f67: plane 10.16x10.16mm, normal (0,0,1), area 84.2mm2, adj f1,f31,f64,f65,f66
  f68: plane 5.08x1.59mm, normal (0,-1,0), area 8.1mm2, adj f8,f34,f70,f71
  f69: plane 5.08x1.59mm, normal (0,1,0), area 8.1mm2, adj f8,f34,f70,f71
  f70: cylinder r=5.08mm len=10.16mm, axis (0,0,1), area 25.3mm2, adj f8,f68,f69,f71
  f71: plane 10.16x10.16mm, normal (0,0,1), area 84.2mm2, adj f0,f34,f68,f69,f70
  f72: cylinder r=15.88mm len=31.75mm, axis (0,0,-1), area 316.7mm2, adj f18,f39
  f73: cylinder r=2.03mm len=5.08mm, axis (0,0,-1), area 64.9mm2, adj f8,f78
  f74: cylinder r=2.03mm len=5.08mm, axis (0,0,-1), area 64.9mm2, adj f8,f77
  f75: cylinder r=2.03mm len=5.08mm, axis (0,0,-1), area 64.9mm2, adj f8,f79
  f76: cylinder r=2.03mm len=5.08mm, axis (0,0,-1), area 64.9mm2, adj f8,f80
  f77: cone r=3.3mm half-angle=45deg, axis (0,0,-1), area 30.1mm2, adj f18,f74
  f78: cone r=3.3mm half-angle=45deg, axis (0,0,-1), area 30.1mm2, adj f18,f73
  f79: cone r=3.3mm half-angle=45deg, axis (0,0,-1), area 30.1mm2, adj f18,f75
  f80: cone r=3.3mm half-angle=45deg, axis (0,0,-1), area 30.1mm2, adj f18,f76
PLACE A rot(axis=(1,0,0),180deg) t=(-4.35,-55.7,11.77)mm
PLACE B rot(axis=(1,0,0),180deg) t=(-4.35,-55.7,75.37)mm
PLACE C t=(-4.35,-55.7,135.3)mm
PLACE D t=(-4.35,-96.47,91.48)mm
PLACE E t=(-4.35,-55.7,82.99)mm
MATE cylindrical E.f2 <-> D.f0  axis (0,0,-1) through (20.04,-96.47,85.37)mm
MATE slider C.f89 <-> E.f72  axis (0,0,1) through (-4.35,-55.7,198.8)mm
MATE cylindrical A.f13 <-> B.f27  axis (0,0,1) through (-4.35,-55.7,-22.52)mm
MATE cylindrical B.f21 <-> E.f5  axis (0,0,1) through (-45.12,-31.32,73.78)mm
